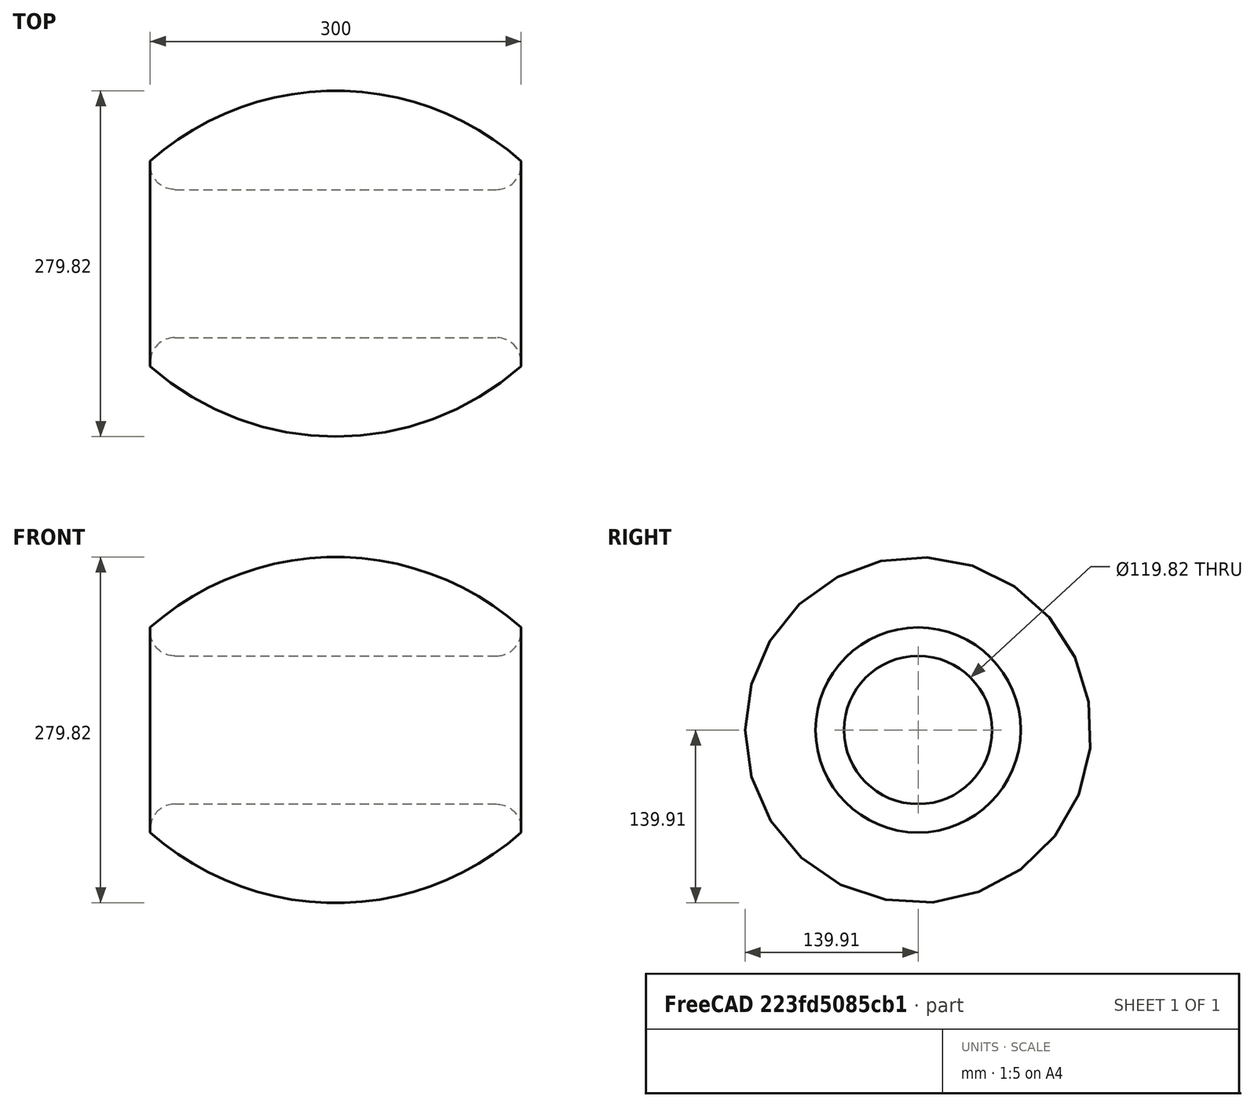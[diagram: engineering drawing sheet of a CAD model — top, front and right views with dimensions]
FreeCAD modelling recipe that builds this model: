
FCSTD DOCUMENT
Label: pr_002
objects: Sketcher::SketchObject×1, PartDesign::Revolution×1
note: 2 computed .brp shape members not serialized (recipe doc carries the construction recipe); baked Part::Feature solids carry a one-line shape summary decoded from their .brp

FEATURE [Sketcher::SketchObject] Sketch
  sketch-geometry (7):
    g0: ArcOfCircle CenterX=9.03839 CenterY=86.0922 CenterZ=0 NormalX=0 NormalY=0 NormalZ=1 Radius=226 StartAngle=3.98661 EndAngle=5.43817
    g1: LineSegment StartX=-140.962 StartY=-82.9522 StartZ=0 EndX=-140.962 EndY=-79.9078 EndZ=0
    g2: LineSegment StartX=159.038 StartY=-82.9522 StartZ=0 EndX=159.038 EndY=-79.9078 EndZ=0
    g3: ArcOfCircle CenterX=-120.962 CenterY=-79.9078 CenterZ=0 NormalX=0 NormalY=0 NormalZ=1 Radius=20 StartAngle=1.5708 EndAngle=3.14159
    g4: ArcOfCircle CenterX=139.038 CenterY=-79.9078 CenterZ=0 NormalX=0 NormalY=0 NormalZ=1 Radius=20 StartAngle=0 EndAngle=1.5708
    g5: LineSegment StartX=-120.962 StartY=-59.9078 StartZ=0 EndX=139.038 EndY=-59.9078 EndZ=0
    g6: LineSegment [constr] StartX=-97.5945 StartY=-139.908 StartZ=0 EndX=79.964 EndY=-139.908 EndZ=0
  constraints (17):
    c: Radius(g0) = 226
    c: Coincident(g1,g0)
    c: Vertical(g1)
    c: Coincident(g2,g0)
    c: Vertical(g2)
    c: Tangent(g3,g1)
    c: Tangent(g4,g2)
    c: Radius(g3) = 20
    c: Radius(g4) = 20
    c: Horizontal(g5)
    c: Tangent(g3,g5)
    c: Tangent(g5,g4)
    c: Equal(g1,g2)
    c: Distance(g0,g0) = 300
    c: Horizontal(g6)
    c: Tangent(g6,g0)
    c: DistanceY(g6,g3) = 80
FEATURE [PartDesign::Revolution] Revolution
  Angle = 360
  Axis = (1,0,0)
  Base = (0,0,0)
  Sketch = -> Sketch
